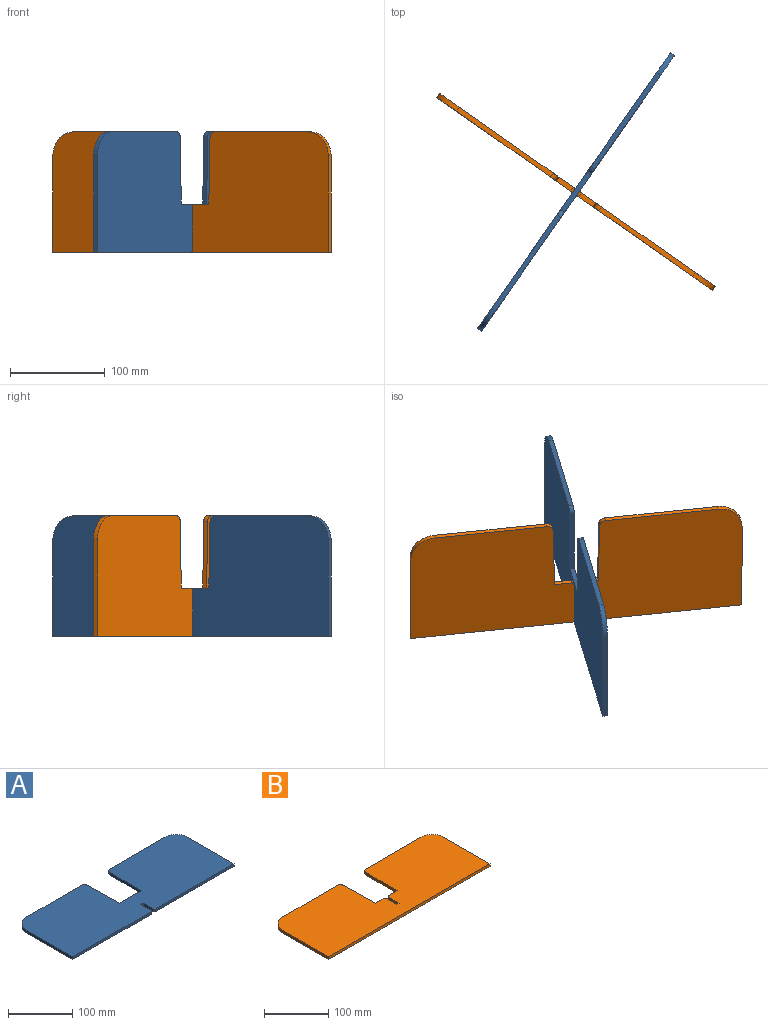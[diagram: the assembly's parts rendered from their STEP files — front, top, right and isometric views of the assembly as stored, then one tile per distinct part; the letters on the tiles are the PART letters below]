
ASSEMBLY  parts=2 mates=1
PART A: 20 faces, bbox 355.6x127x5.1 mm
  f0: plane 46.99x5.08mm, normal (0,1,0), area 238.7mm2, adj f1,f15,f16,f17
  f1: plane 69.99x5.08mm, normal (1,0.02,0), area 355.6mm2, adj f0,f2,f16,f17
  f2: cylinder r=6.35mm len=6.35mm, axis (0,0,-1), area 50mm2, adj f1,f3,f16,f17
  f3: plane 121.03x5.08mm, normal (0,1,0), area 614.8mm2, adj f2,f4,f16,f17
  f4: cylinder r=25.4mm len=25.4mm, axis (0,0,-1), area 202.7mm2, adj f3,f5,f16,f17
  f5: plane 101.6x5.08mm, normal (-1,0,0), area 516.1mm2, adj f4,f6,f16,f17
  f6: plane 172.72x5.08mm, normal (0,-1,0), area 877.4mm2, adj f5,f16,f17,f18
  f7: plane 22.86x5.08mm, normal (1,0,0), area 116.1mm2, adj f8,f16,f17,f18
  f8: plane 5.08x5.08mm, normal (0,-1,0), area 25.8mm2, adj f7,f9,f16,f17
  f9: plane 22.86x5.08mm, normal (-1,0,0), area 116.1mm2, adj f8,f16,f17,f19
  f10: plane 172.72x5.08mm, normal (0,-1,0), area 877.4mm2, adj f11,f16,f17,f19
  f11: plane 101.6x5.08mm, normal (1,0,0), area 516.1mm2, adj f10,f12,f16,f17
  f12: cylinder r=25.4mm len=25.4mm, axis (0,0,-1), area 202.7mm2, adj f11,f13,f16,f17
  f13: plane 121.03x5.08mm, normal (0,1,0), area 614.8mm2, adj f12,f14,f16,f17
  f14: cylinder r=6.35mm len=6.35mm, axis (0,0,-1), area 50mm2, adj f13,f15,f16,f17
  f15: plane 69.99x5.08mm, normal (-1,0.02,0), area 355.6mm2, adj f0,f14,f16,f17
  f16: plane 355.6x127mm, normal (0,0,1), area 41029mm2, adj f0,f1,f2,f3,f4,f5,f6,f7
  f17: plane 355.6x127mm, normal (0,0,-1), area 41029mm2, adj f0,f1,f2,f3,f4,f5,f6,f7
  f18: cylinder r=2.54mm len=5.08mm, axis (0,0,-1), area 20.3mm2, adj f6,f7,f16,f17
  f19: cylinder r=2.54mm len=5.08mm, axis (0,0,-1), area 20.3mm2, adj f9,f10,f16,f17
PART B: 20 faces, bbox 355.6x127x5.1 mm
  f0: plane 121.03x5.08mm, normal (0,1,0), area 614.8mm2, adj f1,f17,f18,f19
  f1: cylinder r=6.35mm len=6.35mm, axis (0,0,-1), area 50mm2, adj f0,f2,f18,f19
  f2: plane 69.99x5.08mm, normal (-1,0.02,0), area 355.6mm2, adj f1,f3,f18,f19
  f3: plane 18.42x5.08mm, normal (0,1,0), area 93.5mm2, adj f2,f4,f18,f19
  f4: cylinder r=2.54mm len=5.08mm, axis (0,0,-1), area 20.3mm2, adj f3,f5,f18,f19
  f5: plane 22.86x5.08mm, normal (-1,0,0), area 116.1mm2, adj f4,f6,f18,f19
  f6: plane 5.08x5.08mm, normal (0,1,0), area 25.8mm2, adj f5,f7,f18,f19
  f7: plane 22.86x5.08mm, normal (1,0,0), area 116.1mm2, adj f6,f8,f18,f19
  f8: cylinder r=2.54mm len=5.08mm, axis (0,0,-1), area 20.3mm2, adj f7,f9,f18,f19
  f9: plane 18.42x5.08mm, normal (0,1,0), area 93.5mm2, adj f8,f10,f18,f19
  f10: plane 69.99x5.08mm, normal (1,0.02,0), area 355.6mm2, adj f9,f11,f18,f19
  f11: cylinder r=6.35mm len=6.35mm, axis (0,0,-1), area 50mm2, adj f10,f12,f18,f19
  f12: plane 121.03x5.08mm, normal (0,1,0), area 614.8mm2, adj f11,f13,f18,f19
  f13: cylinder r=25.4mm len=25.4mm, axis (0,0,-1), area 202.7mm2, adj f12,f14,f18,f19
  f14: plane 101.6x5.08mm, normal (-1,0,0), area 516.1mm2, adj f13,f15,f18,f19
  f15: plane 355.6x5.08mm, normal (0,-1,0), area 1806.4mm2, adj f14,f16,f18,f19
  f16: plane 101.6x5.08mm, normal (1,0,0), area 516.1mm2, adj f15,f17,f18,f19
  f17: cylinder r=25.4mm len=25.4mm, axis (0,0,-1), area 202.7mm2, adj f0,f16,f18,f19
  f18: plane 355.6x127mm, normal (0,0,1), area 41029mm2, adj f0,f1,f2,f3,f4,f5,f6,f7
  f19: plane 355.6x127mm, normal (0,0,-1), area 41029mm2, adj f0,f1,f2,f3,f4,f5,f6,f7
PLACE A rot(axis=(0.81,0.42,0.42),102.3deg) t=(-68.66,-137.25,-83.76)mm
PLACE B rot(axis=(0.91,-0.29,-0.29),95.2deg) t=(-108.78,111,-83.76)mm
MATE fastened A.f8 <-> B.f6  axis (0,0,-1) through (35.41,6.94,-58.36)mm
